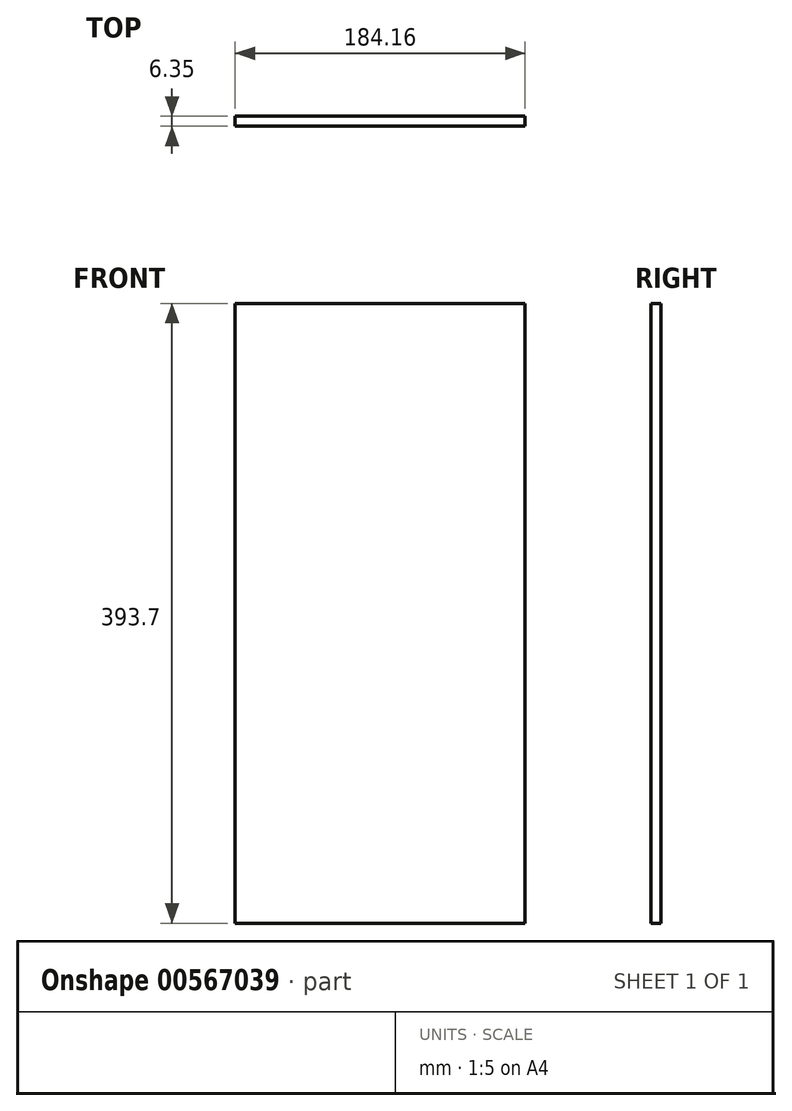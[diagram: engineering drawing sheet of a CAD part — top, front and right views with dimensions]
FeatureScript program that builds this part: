
annotation { "Feature Type Name" : "Feature", "Feature Type Description" : "" }
export const myFeature = defineFeature(function(context is Context, id is Id, definition is map)
    precondition{}
    {
        {
            var Q0;
            Q0=qCreatedBy(makeId("Front.planeOp"),FACE);
            var sketch = newSketch(context, id + "F0", { "sketchPlane" : qUnion([Q0])});
            skLineSegment(sketch, "E0.bottom", {"start": v(92.08, -196.85) * mm, "end": v(-92.07, -196.85) * mm});
            skLineSegment(sketch, "E0.top", {"start": v(92.07, 196.85) * mm, "end": v(-92.08, 196.85) * mm});
            skLineSegment(sketch, "E0.left", {"start": v(92.08, -196.85) * mm, "end": v(92.07, 196.85) * mm});
            skLineSegment(sketch, "E0.right", {"start": v(-92.07, -196.85) * mm, "end": v(-92.08, 196.85) * mm});
            skPoint(sketch, "E0.middle", {"position": v(0, 0) * mm});
            skSolve(sketch);
        }
        {
            var Q0;
            Q0=makeQuery(id+"F0.imprint","IMPRINT",FACE,{"disambiguationData":[TD([[makeQuery(id+"F0.imprint","IMPRINT",EDGE,{"derivedFrom":sQuery(id+"F0.wireOp",EDGE,"E0.bottom")}),-1.0]])]});
            extrude(context, id + "F1", {"entities" : qUnion([Q0]), "depth" : 6.35 * mm, "offsetDistance" : 25.4 * mm});
        }
    });
